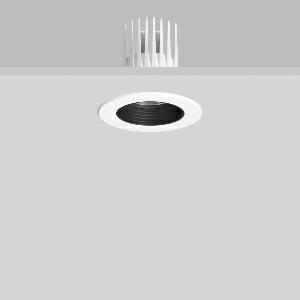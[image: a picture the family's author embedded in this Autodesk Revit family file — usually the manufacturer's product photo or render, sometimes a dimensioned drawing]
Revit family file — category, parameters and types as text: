
# Revit family: heledon_mini_e_901744_002_2_31f9
name_source: partatom
category: Lighting Fixtures
units: mm (PartAtom-declared; Revit-internal decimal feet)

## family parameters
Cut with Voids When Loaded = No
Host = Face
Light Source = No
Part Type = Normal
Room Calculation Point = No
Round Connector Dimension = Use Diameter
Shared = No

## types (1)
- HELEDON mini E (1 x LED Modul 927, 2000 lm, 2700)
    Apparent Load = 20 VA
    Approval mark = CE
    CIE Flux Codes = 96 100 100 100 100
    Color Rendering = 92
    Color Temperature = 2700
    Default Elevation = 1800 mm
    Description = Series: HELEDON mini
Round recessed downlight. Housing: die-cast aluminium, powder-coated. Black plastic ring and recessed LED to prevent glare from the side. Optical assembly with lens made of plastic (polycarbonate) for the best homogeneous light distribution - can be changed without tools. Best colour rendering index Ra>90. Suitable for Recessed ceiling mounting. Installation without tools thanks to spring fastening system. Including separate LED converter with connecting cable 600 mm.High quality converter without flickering and stroboscopic effect. Through-wiring box (5 pole) available as accessory. The following accessories can be mounted without use of tools: interchangeable lenses, decorative glasses, honeycomb louvre, clear and frosted diffusers, white interchangeable plastic ring. 
Colour: traffic white, matt (RAL 9016)
Diameter: 124 mm
Height: 3 mm
Cut-out diameter: 114 mm
Recess height: 170 mm
Luminaire: recess height: 120 mm
Lamp: LED
Socket: without socket
Colour temperature: 2700K
Colour rendering index (CRI): 92
System power: 20 W
Rated luminous flux: 2000 lm
Luminous efficiency: 100 lm/W
Control gear: Regulated power supply
Protection class: II
Type of protection: IP 20
    Height = 0 mm  [stored 0 ft]
    Lamp = 1 x LED Modul 927
    Lamp Light Flux = 2000 lm
    Lamp count = 1
    Length = 124 mm  [stored 0.406824 ft]
    Lifetime = 50000 h
    Luminous efficacy = 100 lm/W
    Manufacturer = RZB
    ModVariant = No
    Model = 901744.002.2
    Mounting Place = Ceiling
    Mounting Type = Recessed
    Number of Poles = 1
    OnlyDefault = Yes
    Power Factor = 1
    Product Name = HELEDON mini E
    Product group = Recessed downlights
    ProductGroupID = 402
    Protection Class = Protection class II
    Protection Degree = IP 20
    RLX_Detail_Level = 1
    RLX_Emergency_Light_Flux = 0 lm
    RLX_Emergency_Type = 0
    RLX_Emergency_Type_DB = No
    RlxData = <blob elided: 125073 chars, md5=52297cc7>
    Socket = socket
    Standby Power = 0 W
    System Light Flux = 2000 lm
    System Power = 20 W
    Type Comments = Product without accessories
    Type Image = 901656.002.jpg
    URL = http://relux.com
    VarID = ---
    Voltage = 230 V
    Voltage Range = 220-240 V
    Weight = 0.00 kg
    Width = 0 mm  [stored 0 ft]

note: [stored X ft] marks values corroborated as IEEE doubles in the binary element streams (Revit-internal decimal feet)

## geometry (parser evidence)
native form markers: Blend x4, Sweep x9
no freeform markers — native parametric forms only
